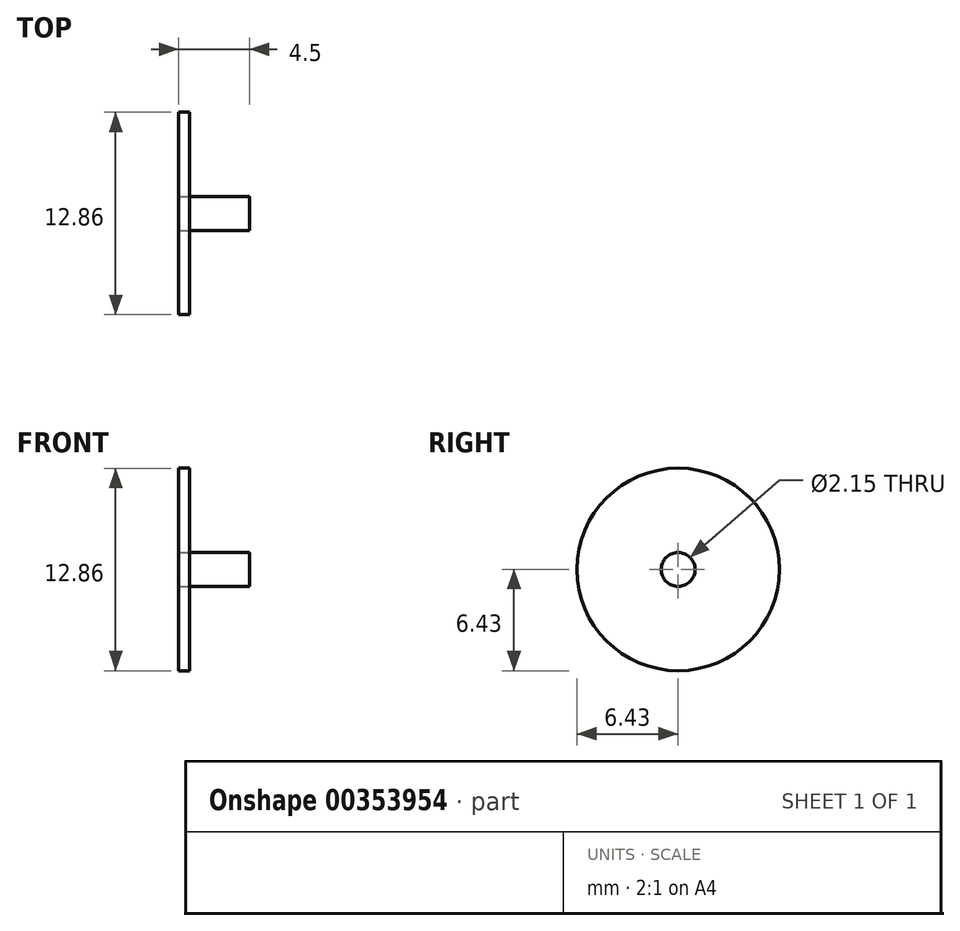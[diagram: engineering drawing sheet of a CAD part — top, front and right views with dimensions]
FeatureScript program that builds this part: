
annotation { "Feature Type Name" : "Feature", "Feature Type Description" : "" }
export const myFeature = defineFeature(function(context is Context, id is Id, definition is map)
    precondition{}
    {
        {
            var Q0;
            Q0=qCreatedBy(makeId("Right.planeOp"),FACE);
            var sketch = newSketch(context, id + "F0", { "sketchPlane" : qUnion([Q0])});
            skCircle(sketch, "E0", {"center": v(0, 0) * mm, "radius": 1.08 * mm});
            skSolve(sketch);
        }
        {
            var Q0;
            Q0=makeQuery(id+"F0.imprint","IMPRINT",FACE,{"disambiguationData":[TD([[makeQuery(id+"F0.imprint","IMPRINT",EDGE,{"derivedFrom":sQuery(id+"F0.wireOp",EDGE,"E0")}),1.0]])]});
            extrude(context, id + "F1", {"entities" : qUnion([Q0]), "depth" : 3.8 * mm});
        }
        {
            var Q0;
            Q0=makeQuery(id+"F1.opExtrude","CAP_FACE",FACE,{"disambiguationData":[OSD([sQuery(id+"F0.wireOp",EDGE,"E0")])],"isStart":true});
            var sketch = newSketch(context, id + "F2", { "sketchPlane" : qUnion([Q0])});
            skCircle(sketch, "E1", {"center": v(0, 0) * mm, "radius": 6.43 * mm});
            skSolve(sketch);
        }
        {
            var Q0;
            Q0=makeQuery(id+"F2.imprint","IMPRINT",FACE,{"disambiguationData":[TD([[makeQuery(id+"F2.imprint","IMPRINT",EDGE,{"derivedFrom":sQuery(id+"F2.wireOp",EDGE,"E1")}),1.0]])]});
            extrude(context, id + "F3", {"entities" : qUnion([Q0]), "depth" : 0.7 * mm});
        }
    });
